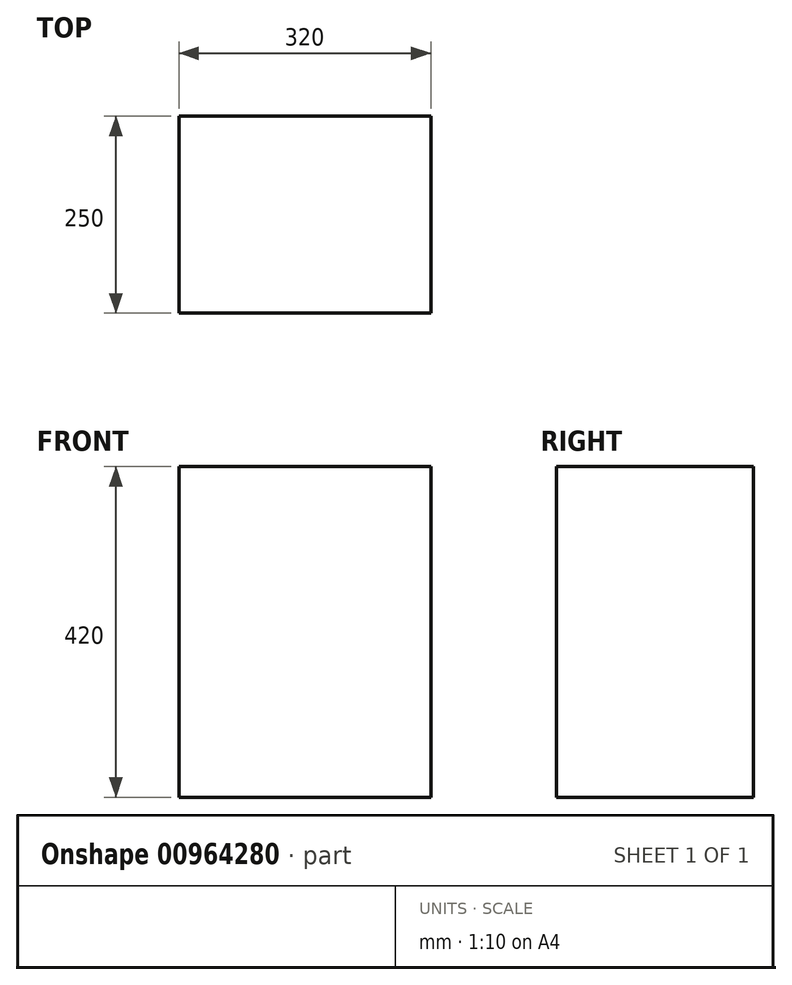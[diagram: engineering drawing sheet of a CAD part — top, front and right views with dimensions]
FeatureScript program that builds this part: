
annotation { "Feature Type Name" : "Feature", "Feature Type Description" : "" }
export const myFeature = defineFeature(function(context is Context, id is Id, definition is map)
    precondition{}
    {
        {
            var Q0;
            Q0=qCreatedBy(makeId("Front.planeOp"),FACE);
            var sketch = newSketch(context, id + "F0", { "sketchPlane" : qUnion([Q0])});
            skLineSegment(sketch, "E0.bottom", {"start": v(-160, 0) * mm, "end": v(160, 0) * mm});
            skLineSegment(sketch, "E0.top", {"start": v(-160, 420) * mm, "end": v(160, 420) * mm});
            skLineSegment(sketch, "E0.left", {"start": v(-160, 0) * mm, "end": v(-160, 420) * mm});
            skLineSegment(sketch, "E0.right", {"start": v(160, 0) * mm, "end": v(160, 420) * mm});
            skSolve(sketch);
        }
        {
            var Q0;
            Q0 = qSketchRegion(id + "F0", true);
            extrude(context, id + "F1", {"entities" : qUnion([Q0]), "depth" : 250 * mm, "offsetDistance" : 25 * mm});
        }
    });
